# Revit family: rs_pro_connect_r30_057145
name_source: partatom
category: Leuchten
revit_build: Autodesk Revit 2016 (Build: 20190508_0715(x64)
units: mm (PartAtom-declared; Revit-internal decimal feet)

## family parameters
Basisbauteil = Fläche
Beim Laden mit Abzugskörper schneiden = Nein
Bemaßung runder Anschluss = Durchmesser verwenden
Gemeinsam genutzt = Nein
Lichtquelle = Nein
Raumberechnungspunkt = Nein
Teiletyp = Normal

## types (1)
- RS PRO Connect R30 (1 x , 3120 lm, 3000 K)
    Beschreibung = Dimensions (Ø x H): 420 x 55 mm; Mains power supply: 220 – 240 V / 50 – 60 Hz; Sensor Technology: High frequency; Transmitter power: < 1 mW; HF-system: 5,8 GHz; Output: 24,5 W; Interconnection: Yes; Type of interconnection: Master/slave; Luminous flux: 3120 lm; Colour temperature: 3000 K; Colour variation LED: SDCM3; Colour Rendering Index CRI: 80-89; With lamp: Yes, STEINEL LED system; Lamp: LED cannot be replaced; LED life expectancy (max. °C): 55000 h; LED life expectancy (25 °C): 60000 h; Drop in luminous flux in accordance with LM80: L80B50; Base: without; LED cooling system: Passive Thermo Control; With motion detector: Yes; Detection: also through glass, wood and stud walls; Detection angle: 360 °; Angle of aperture: 160 °; Capability of masking out individual segments: Yes; Electronic scalability: Yes; Mechanical scalability: No; Reach, radial: Ø 10 m (79 m²); Reach, tangential: Ø 10 m (79 m²); Main light adjustable: 50 - 100 %; Continuous light: selectable; Photo-cell controller: Yes; Twilight setting: 2 – 2000 lx; Time setting: 5 sec – 30 min; Basic light level function: Yes; Basic light level function, detail: LED Backlight; Basic light level function time: 10-30 min, all night; Functions: Group parameterisation, Manual ON / ON-OFF, Master/slave override, Neighbouring-group function, Presence function, Backlight; Soft light start: Yes; Impact resistance: IK07; IP-rating: IP40; Protection class: II; Ambient temperature: -20 – 40 °C; Housing material: Plastic; Cover material: PC, opal; Manufacturer's Warranty: 5 years; Settings via: Bluetooth; With remote control: No; Version: warm white; PU1, EAN: 4007841057145
    CIE Flux Codes = 45 76 94 95 100
    Color Rendering = 80-89
    Color Temperature = 3000 K
    Frequency = 60 Hz, 50 Hz
    Height = 0 mm  [stored 0 ft]
    Hersteller = Steinel
    Lamp Light Flux = 3120 lm
    Lamp count = 1
    Lampe = 1 x
    Length = 420 mm
    Luminous efficacy = 0 lm/W
    ModVariant = Nein
    Modell = 057145
    Mounting Type = Surface mounted
    Number of Poles = 1
    OnlyDefault = Ja
    Power Factor = 1
    Product Name = RS PRO Connect R30
    Product group = Sensor-switched indoor light
    ProductGroupID = 30
    Protection Class = Protection class II
    Protection Degree = IP 40
    RlxData = <blob elided: 182709 chars, md5=23ac3159>
    Scheinlast = 0 VA
    Socket = socket
    Standby Power = 0 W
    System Light Flux = 0 lm
    System Power = 0 W
    Typenbild = produkt1_057145.jpg
    Typenkommentare = Product without accessories
    URL = http://relux.com
    VarID = ---
    Voltage = 0 V
    Vorgabe-Ansicht = 1800 mm
    Weight = 0.00 kg
    Width = 0 mm  [stored 0 ft]

note: [stored X ft] marks values corroborated as IEEE doubles in the binary element streams (Revit-internal decimal feet)

## geometry (parser evidence)
native form markers: Blend x4, Sweep x15
no freeform markers — native parametric forms only
